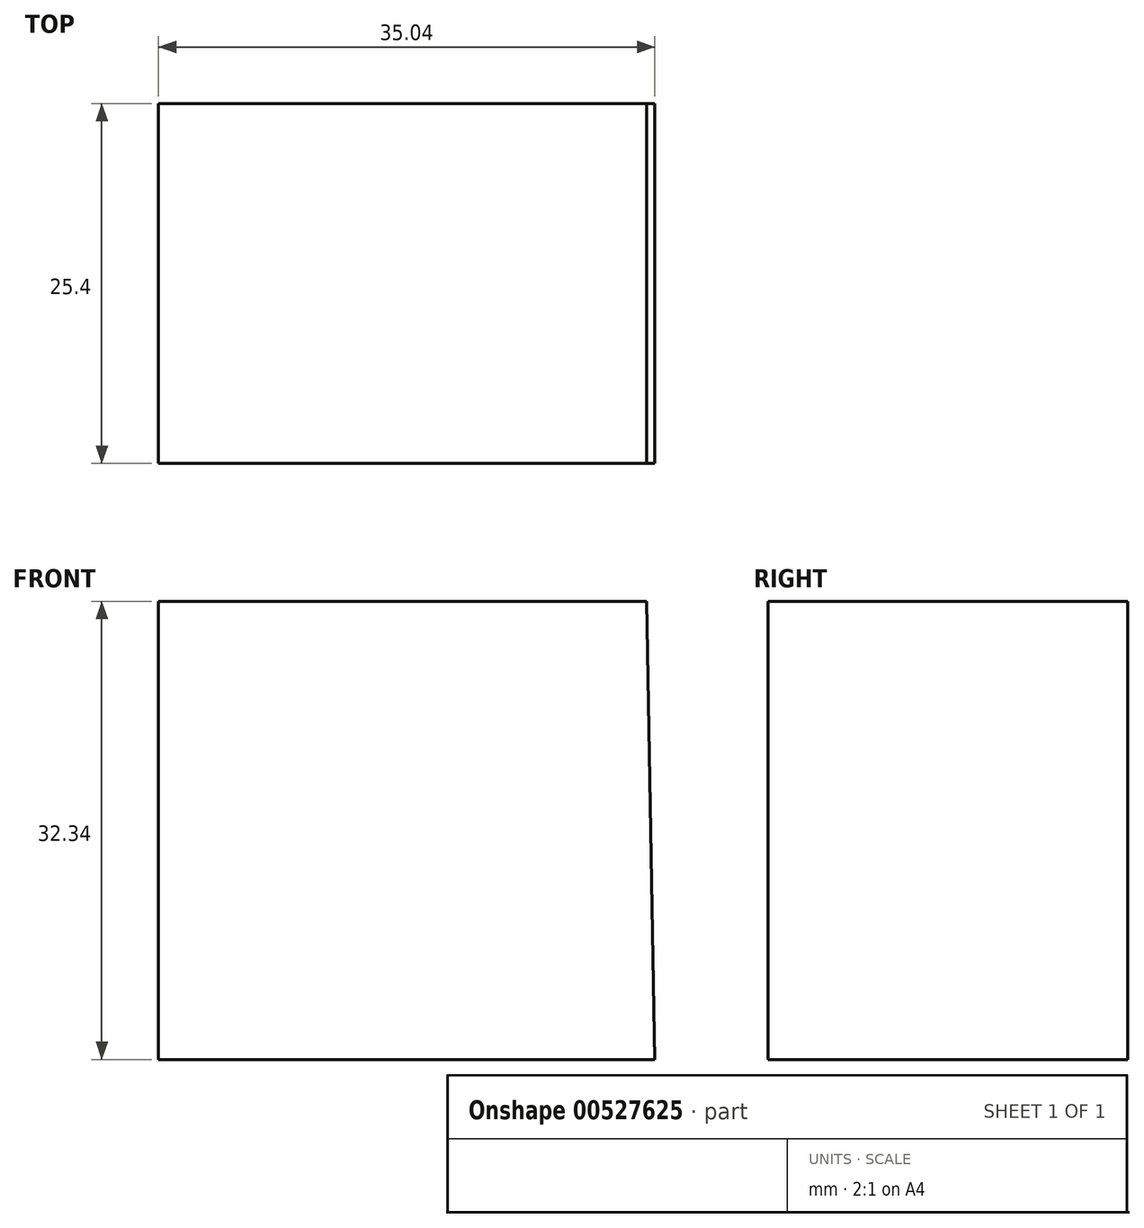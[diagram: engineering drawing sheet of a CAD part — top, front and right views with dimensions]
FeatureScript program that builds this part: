
annotation { "Feature Type Name" : "Feature", "Feature Type Description" : "" }
export const myFeature = defineFeature(function(context is Context, id is Id, definition is map)
    precondition{}
    {
        {
            var Q0;
            Q0=qCreatedBy(makeId("Front.planeOp"),FACE);
            var sketch = newSketch(context, id + "F0", { "sketchPlane" : qUnion([Q0])});
            skLineSegment(sketch, "E0", {"start": v(0, 0) * mm, "end": v(35.04, 0) * mm});
            skLineSegment(sketch, "E1", {"start": v(0, 32.34) * mm, "end": v(0, 0) * mm});
            skLineSegment(sketch, "E2", {"start": v(0, 32.34) * mm, "end": v(34.47, 32.34) * mm});
            skLineSegment(sketch, "E3", {"start": v(34.47, 32.34) * mm, "end": v(35.04, 0) * mm});
            skSolve(sketch);
        }
        {
            var Q0;
            Q0 = qSketchRegion(id + "F0", true);
            extrude(context, id + "F1", {"entities" : qUnion([Q0]), "depth" : 25.4 * mm, "offsetDistance" : 25.4 * mm});
        }
    });
